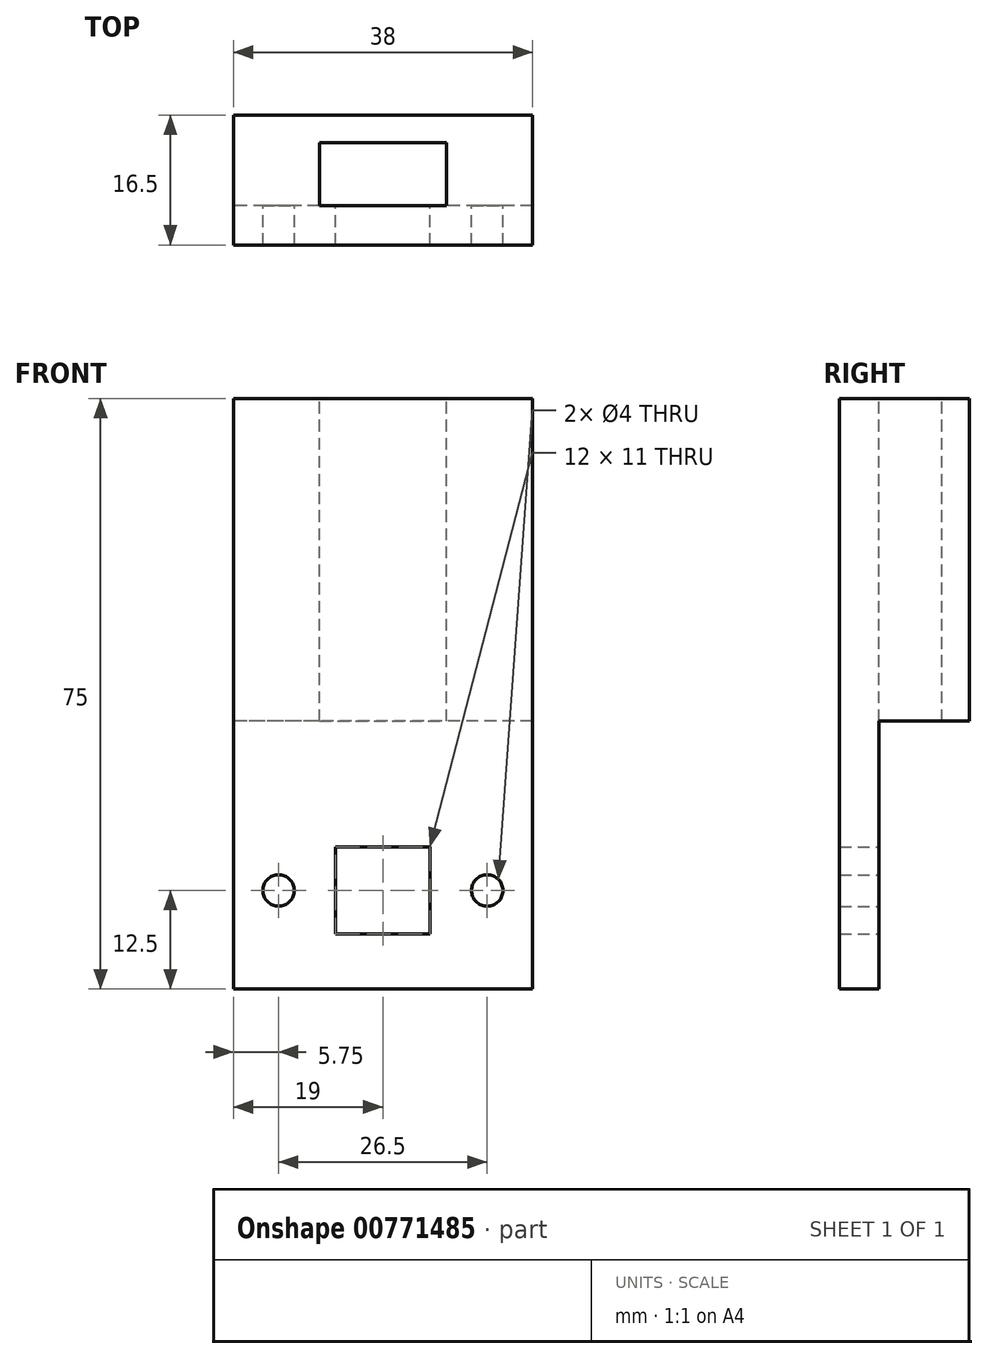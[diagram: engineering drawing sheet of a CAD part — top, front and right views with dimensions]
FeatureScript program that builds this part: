
annotation { "Feature Type Name" : "Feature", "Feature Type Description" : "" }
export const myFeature = defineFeature(function(context is Context, id is Id, definition is map)
    precondition{}
    {
        {
            var Q0;
            Q0=qCreatedBy(makeId("Front.planeOp"),FACE);
            var sketch = newSketch(context, id + "F0", { "sketchPlane" : qUnion([Q0])});
            skCircle(sketch, "E0", {"center": v(0, 0) * mm, "radius": 2.5 * mm});
            skCircle(sketch, "E1", {"center": v(-13.25, 0) * mm, "radius": 2 * mm});
            skCircle(sketch, "E2", {"center": v(13.25, 0) * mm, "radius": 2 * mm});
            skLineSegment(sketch, "E3.bottom", {"start": v(19, -12.5) * mm, "end": v(-19, -12.5) * mm});
            skLineSegment(sketch, "E3.top", {"start": v(19, 12.5) * mm, "end": v(-19, 12.5) * mm});
            skLineSegment(sketch, "E3.left", {"start": v(19, -12.5) * mm, "end": v(19, 12.5) * mm});
            skLineSegment(sketch, "E3.right", {"start": v(-19, -12.5) * mm, "end": v(-19, 12.5) * mm});
            skLineSegment(sketch, "E4", {"start": v(19, -3.5) * mm, "end": v(8, -3.5) * mm});
            skLineSegment(sketch, "E5", {"start": v(8, -3.5) * mm, "end": v(8, 0) * mm});
            skLineSegment(sketch, "E6", {"start": v(8, 0) * mm, "end": v(-8, 0) * mm});
            skLineSegment(sketch, "E7", {"start": v(-8, 0) * mm, "end": v(-8, 3.5) * mm});
            skLineSegment(sketch, "E8", {"start": v(-8, 3.5) * mm, "end": v(-19, 3.5) * mm});
            skSolve(sketch);
        }
        {
            var Q0;
            Q0=qCreatedBy(makeId("Front.planeOp"),FACE);
            var sketch = newSketch(context, id + "F1", { "sketchPlane" : qUnion([Q0])});
            skLineSegment(sketch, "E9.bottom", {"start": v(6, -5.5) * mm, "end": v(-6, -5.5) * mm});
            skLineSegment(sketch, "E9.top", {"start": v(6, 5.5) * mm, "end": v(-6, 5.5) * mm});
            skLineSegment(sketch, "E9.left", {"start": v(6, -5.5) * mm, "end": v(6, 5.5) * mm});
            skLineSegment(sketch, "E9.right", {"start": v(-6, -5.5) * mm, "end": v(-6, 5.5) * mm});
            skPoint(sketch, "E9.middle", {"position": v(0, 0) * mm});
            skSolve(sketch);
        }
        {
            var Q0;
            Q0=makeQuery(id+"F0.imprint","IMPRINT",FACE,{"disambiguationData":[TD([[makeQuery(id+"F0.imprint","IMPRINT",EDGE,{"derivedFrom":sQuery(id+"F0.wireOp",EDGE,"E2")}),-1.0]])]});
            var Q1;
            Q1=makeQuery(id+"F0.imprint","IMPRINT",FACE,{"disambiguationData":[TD([[makeQuery(id+"F0.imprint","IMPRINT",EDGE,{"derivedFrom":sQuery(id+"F0.wireOp",EDGE,"E1")}),-1.0]])]});
            extrude(context, id + "F2", {"entities" : qUnion([Q0, Q1]), "depth" : 5 * mm, "offsetDistance" : 25 * mm});
        }
        {
            var Q0;
            Q0=makeQuery(id+"F1.imprint","IMPRINT",FACE,{"disambiguationData":[TD([[makeQuery(id+"F1.imprint","IMPRINT",EDGE,{"derivedFrom":sQuery(id+"F1.wireOp",EDGE,"E9.bottom")}),-1.0]])]});
            extrude(context, id + "F3", {"entities" : qUnion([Q0]), "operationType" : NewBodyOperationType.REMOVE, "depth" : 50.9 * mm, "offsetDistance" : 25 * mm});
        }
        {
            var Q0;
            Q0=makeQuery(id+"F2.opExtrude","SWEPT_FACE",FACE,{"disambiguationData":[OSD([sQuery(id+"F0.wireOp",EDGE,"E3.top")])]});
            var sketch = newSketch(context, id + "F4", { "sketchPlane" : qUnion([Q0])});
            skLineSegment(sketch, "E10.bottom", {"start": v(19, -5) * mm, "end": v(-19, -5) * mm});
            skLineSegment(sketch, "E10.top", {"start": v(19, 15) * mm, "end": v(-19, 15) * mm});
            skLineSegment(sketch, "E10.left", {"start": v(19, -5) * mm, "end": v(19, 15) * mm});
            skLineSegment(sketch, "E10.right", {"start": v(-19, -5) * mm, "end": v(-19, 15) * mm});
            skSolve(sketch);
        }
        {
            var Q0;
            {var subQ0=sQuery(id+"F4.wireOp",EDGE,"E10.top");Q0=makeQuery(id+"F4.imprint","IMPRINT",FACE,{"disambiguationData":[TD([[makeQuery(id+"F4.imprint","IMPRINT",EDGE,{"derivedFrom":subQ0}),1.0]])]});}
            var Q1;
            {var subQ0=sQuery(id+"F4.wireOp",EDGE,"E10.bottom");Q1=makeQuery(id+"F4.imprint","IMPRINT",FACE,{"disambiguationData":[TD([[makeQuery(id+"F4.imprint","IMPRINT",EDGE,{"derivedFrom":subQ0}),-1.0]])]});}
            extrude(context, id + "F5", {"entities" : qUnion([Q0, Q1]), "operationType" : NewBodyOperationType.ADD, "depth" : 50 * mm, "offsetDistance" : 25 * mm});
        }
        {
            var Q0;
            Q0=makeQuery(id+"F5.opExtrude","CAP_FACE",FACE,{"disambiguationData":[OSD([sQuery(id+"F4.wireOp",EDGE,"E10.bottom"),sQuery(id+"F4.wireOp",EDGE,"E10.top"),sQuery(id+"F4.wireOp",EDGE,"E10.left"),sQuery(id+"F4.wireOp",EDGE,"E10.right")])],"isStart":true});
            extrude(context, id + "F6", {"entities" : qUnion([Q0]), "operationType" : NewBodyOperationType.REMOVE, "oppositeDirection" : true, "depth" : 9 * mm, "offsetDistance" : 25 * mm});
        }
        {
            var Q0;
            Q0=makeQuery(id+"F5.opExtrude","CAP_FACE",FACE,{"disambiguationData":[OSD([sQuery(id+"F4.wireOp",EDGE,"E10.bottom"),sQuery(id+"F4.wireOp",EDGE,"E10.top"),sQuery(id+"F4.wireOp",EDGE,"E10.left"),sQuery(id+"F4.wireOp",EDGE,"E10.right")])],"isStart":false});
            var sketch = newSketch(context, id + "F7", { "sketchPlane" : qUnion([Q0])});
            skLineSegment(sketch, "E11.bottom", {"start": v(-8.05, 0) * mm, "end": v(8.05, 0) * mm});
            skLineSegment(sketch, "E11.top", {"start": v(-8.05, 8) * mm, "end": v(8.05, 8) * mm});
            skLineSegment(sketch, "E11.left", {"start": v(-8.05, 0) * mm, "end": v(-8.05, 8) * mm});
            skLineSegment(sketch, "E11.right", {"start": v(8.05, 0) * mm, "end": v(8.05, 8) * mm});
            skPoint(sketch, "E11.middle", {"position": v(0, 4) * mm});
            skSolve(sketch);
        }
        {
            var Q0;
            Q0=makeQuery(id+"F7.imprint","IMPRINT",FACE,{"disambiguationData":[TD([[makeQuery(id+"F7.imprint","IMPRINT",EDGE,{"derivedFrom":sQuery(id+"F7.wireOp",EDGE,"E11.bottom")}),1.0]])]});
            extrude(context, id + "F8", {"entities" : qUnion([Q0]), "operationType" : NewBodyOperationType.REMOVE, "oppositeDirection" : true, "depth" : 59.7 * mm, "offsetDistance" : 25 * mm});
        }
        {
            var Q0;
            Q0=makeQuery(id+"F5.opExtrude","SWEPT_FACE",FACE,{"disambiguationData":[OSD([sQuery(id+"F4.wireOp",EDGE,"E10.top")])]});
            extrude(context, id + "F9", {"entities" : qUnion([Q0]), "operationType" : NewBodyOperationType.REMOVE, "oppositeDirection" : true, "depth" : 3.5 * mm, "offsetDistance" : 25 * mm});
        }
    });
